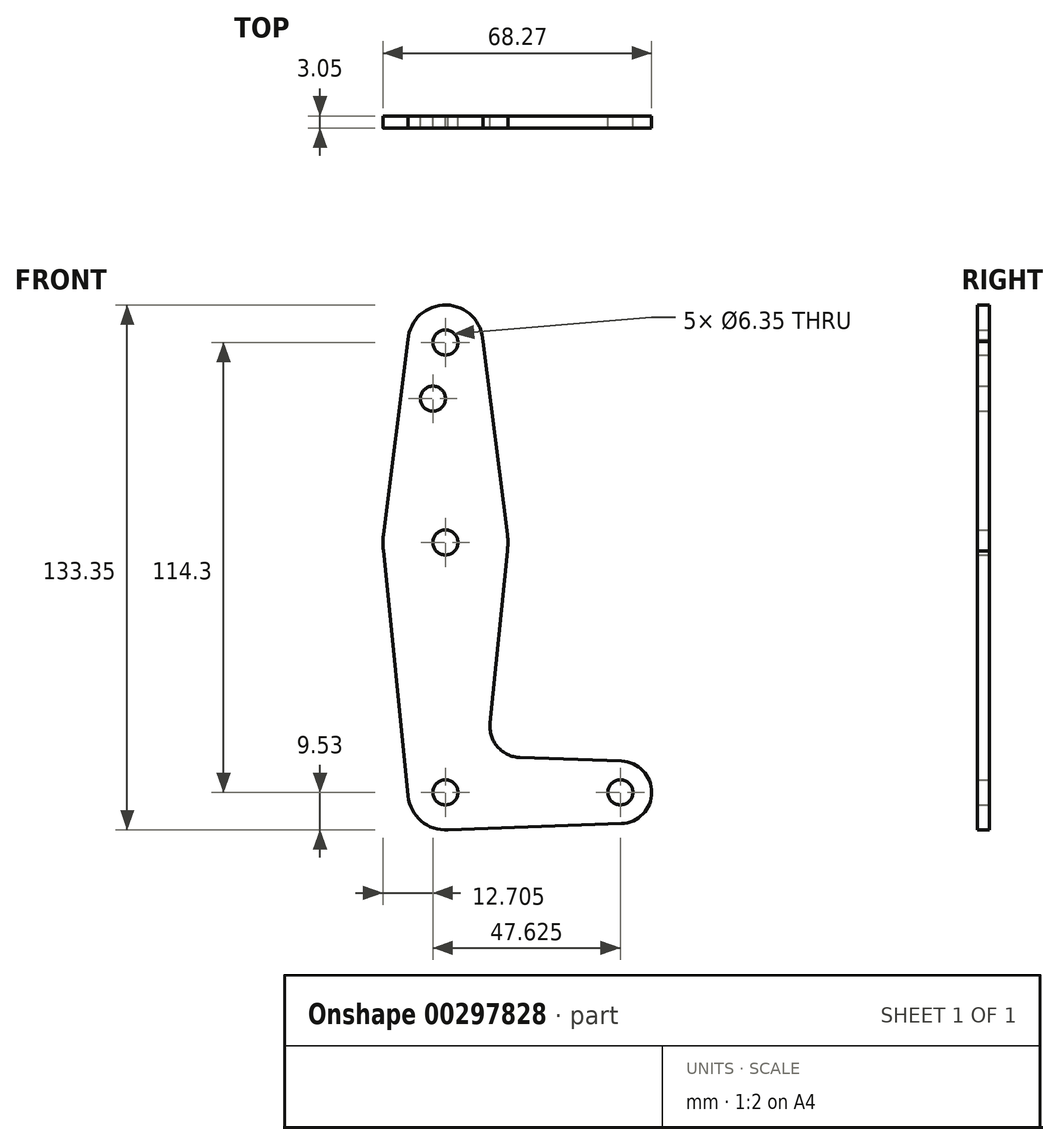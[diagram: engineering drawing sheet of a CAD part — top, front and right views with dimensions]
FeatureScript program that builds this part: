
annotation { "Feature Type Name" : "Feature", "Feature Type Description" : "" }
export const myFeature = defineFeature(function(context is Context, id is Id, definition is map)
    precondition{}
    {
        {
            var Q0;
            Q0=qCreatedBy(makeId("Front.planeOp"),FACE);
            var sketch = newSketch(context, id + "F0", { "sketchPlane" : qUnion([Q0])});
            skLineSegment(sketch, "E0", {"start": v(0, 0) * mm, "end": v(0, 114.3) * mm, "construction": true});
            skLineSegment(sketch, "E1", {"start": v(0, 0) * mm, "end": v(44.45, 0) * mm, "construction": true});
            skCircle(sketch, "E2", {"center": v(0, 0) * mm, "radius": 9.53 * mm});
            skCircle(sketch, "E3", {"center": v(0, 114.3) * mm, "radius": 9.53 * mm});
            skCircle(sketch, "E4", {"center": v(44.45, 0) * mm, "radius": 7.94 * mm});
            skCircle(sketch, "E5", {"center": v(0, 63.5) * mm, "radius": 15.88 * mm});
            skLineSegment(sketch, "E6", {"start": v(-9.38, 115.98) * mm, "end": v(-15.75, 65.49) * mm});
            skLineSegment(sketch, "E7", {"start": v(9.52, 114.52) * mm, "end": v(15.75, 65.5) * mm});
            skLineSegment(sketch, "E8", {"start": v(-15.82, 62.23) * mm, "end": v(-9.48, -0.95) * mm});
            skLineSegment(sketch, "E9", {"start": v(15.84, 62.51) * mm, "end": v(11.34, 17.59) * mm});
            skLineSegment(sketch, "E10", {"start": v(18.96, 8.85) * mm, "end": v(44.73, 7.93) * mm});
            skLineSegment(sketch, "E11", {"start": v(0, -9.53) * mm, "end": v(44.73, -7.93) * mm});
            skCircle(sketch, "E12", {"center": v(0, 114.3) * mm, "radius": 3.18 * mm});
            skCircle(sketch, "E13", {"center": v(-3.18, 100.03) * mm, "radius": 3.18 * mm});
            skCircle(sketch, "E14", {"center": v(0, 63.5) * mm, "radius": 3.18 * mm});
            skCircle(sketch, "E15", {"center": v(0, 0) * mm, "radius": 3.18 * mm});
            skCircle(sketch, "E16", {"center": v(44.45, 0) * mm, "radius": 3.18 * mm});
            skPoint(sketch, "E17.newPointA", {"position": v(0, 9.53) * mm});
            skPoint(sketch, "E17.newPointB", {"position": v(9.48, -0.95) * mm});
            skArc(sketch, "E17.filletArc", {"start": v(11.34, 17.59) * mm, "mid": v(13.26, 11.57) * mm, "end": v(18.96, 8.85) * mm});
            skSolve(sketch);
        }
        {
            var Q0;
            Q0 = qSketchRegion(id + "F0", true);
            extrude(context, id + "F1", {"entities" : qUnion([Q0]), "depth" : 3.05 * mm});
        }
    });
